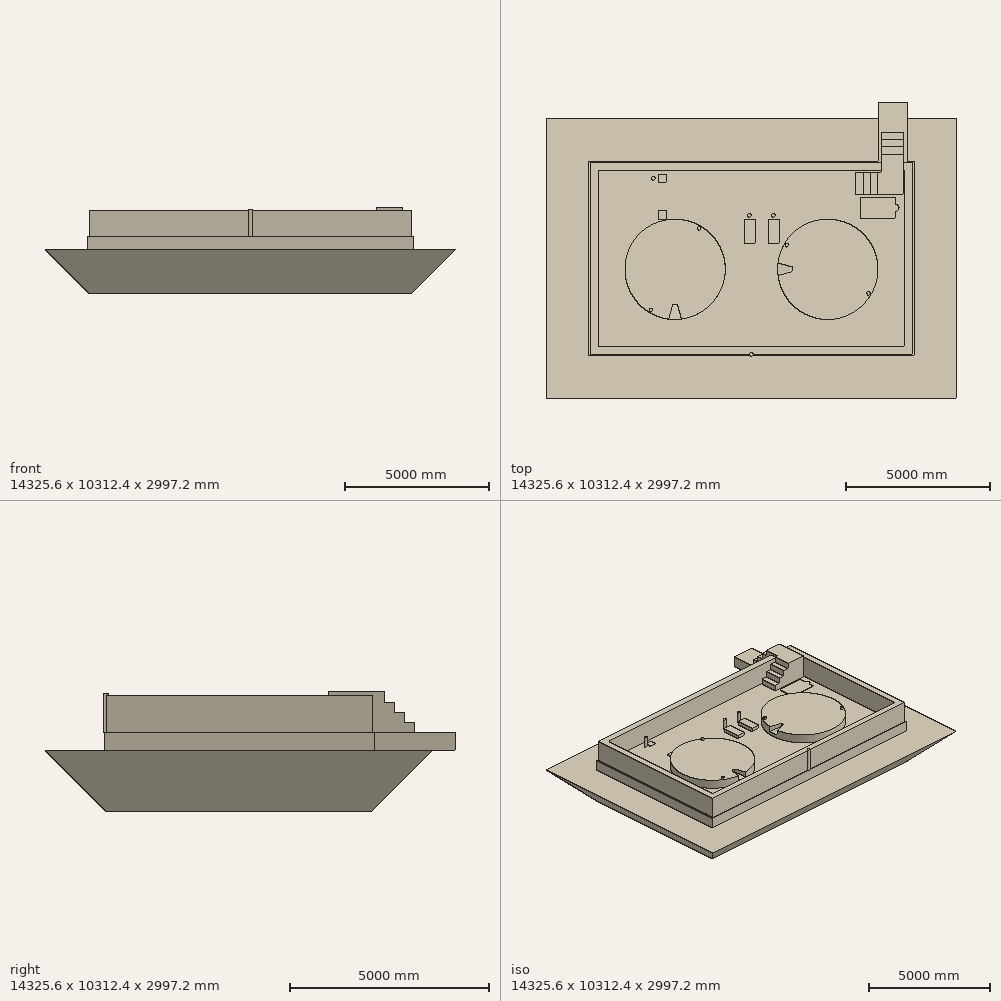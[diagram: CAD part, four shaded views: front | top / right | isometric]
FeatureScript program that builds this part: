
annotation { "Feature Type Name" : "Feature", "Feature Type Description" : "" }
export const myFeature = defineFeature(function(context is Context, id is Id, definition is map)
    precondition{}
    {
        {
            var Q0;
            Q0=qCreatedBy(makeId("Top.planeOp"),FACE);
            var sketch = newSketch(context, id + "F0", { "sketchPlane" : qUnion([Q0])});
            skLineSegment(sketch, "E0.bottom", {"start": v(5638.8, 3352.8) * mm, "end": v(-5638.8, 3352.8) * mm});
            skLineSegment(sketch, "E0.top", {"start": v(5638.8, -3352.8) * mm, "end": v(-5638.8, -3352.8) * mm});
            skLineSegment(sketch, "E0.left", {"start": v(5638.8, 3352.8) * mm, "end": v(5638.8, -3352.8) * mm});
            skLineSegment(sketch, "E0.right", {"start": v(-5638.8, 3352.8) * mm, "end": v(-5638.8, -3352.8) * mm});
            skPoint(sketch, "E0.middle", {"position": v(0, 0) * mm});
            skSolve(sketch);
        }
        {
            var Q0;
            Q0 = qSketchRegion(id + "F0", true);
            extrude(context, id + "F1", {"entities" : qUnion([Q0]), "oppositeDirection" : true, "depth" : 457.2 * mm});
        }
        {
            var Q0;
            Q0=makeQuery(id+"F1.opExtrude","CAP_FACE",FACE,{"disambiguationData":[OSD([sQuery(id+"F0.wireOp",EDGE,"E0.bottom"),sQuery(id+"F0.wireOp",EDGE,"E0.top"),sQuery(id+"F0.wireOp",EDGE,"E0.left"),sQuery(id+"F0.wireOp",EDGE,"E0.right")])],"isStart":true});
            var sketch = newSketch(context, id + "F2", { "sketchPlane" : qUnion([Q0])});
            skLineSegment(sketch, "E1.0.0", {"start": v(-5638.8, -3352.8) * mm, "end": v(5638.8, -3352.8) * mm});
            skLineSegment(sketch, "E1.0.1", {"start": v(5638.8, -3352.8) * mm, "end": v(5638.8, 3352.8) * mm});
            skLineSegment(sketch, "E1.0.2", {"start": v(5638.8, 3352.8) * mm, "end": v(-5638.8, 3352.8) * mm});
            skLineSegment(sketch, "E1.0.3", {"start": v(-5638.8, 3352.8) * mm, "end": v(-5638.8, -3352.8) * mm});
            skLineSegment(sketch, "E2.0", {"start": v(-5334, -3048) * mm, "end": v(5334, -3048) * mm});
            skLineSegment(sketch, "E2.1", {"start": v(-5334, 3048) * mm, "end": v(-5334, -3048) * mm});
            skLineSegment(sketch, "E2.2", {"start": v(5334, 3048) * mm, "end": v(-5334, 3048) * mm});
            skLineSegment(sketch, "E2.3", {"start": v(5334, -3048) * mm, "end": v(5334, 3048) * mm});
            skSolve(sketch);
        }
        {
            var Q0;
            Q0 = qSketchRegion(id + "F2", true);
            extrude(context, id + "F3", {"entities" : qUnion([Q0]), "depth" : 914.4 * mm});
        }
        {
            var Q0;
            Q0=makeQuery(id+"F1.opExtrude","CAP_FACE",FACE,{"disambiguationData":[OSD([sQuery(id+"F0.wireOp",EDGE,"E0.bottom"),sQuery(id+"F0.wireOp",EDGE,"E0.top"),sQuery(id+"F0.wireOp",EDGE,"E0.left"),sQuery(id+"F0.wireOp",EDGE,"E0.right")])],"isStart":true});
            var sketch = newSketch(context, id + "F4", { "sketchPlane" : qUnion([Q0])});
            skCircle(sketch, "E3.cCircle", {"center": v(-2667, -381) * mm, "radius": 1676.4 * mm, "construction": true});
            skLineSegment(sketch, "E3.0", {"start": v(-1972.61, 1295.4) * mm, "end": v(-990.6, 313.39) * mm, "construction": true});
            skLineSegment(sketch, "E3.1", {"start": v(-990.6, 313.39) * mm, "end": v(-990.6, -1075.39) * mm, "construction": true});
            skLineSegment(sketch, "E3.2", {"start": v(-990.6, -1075.39) * mm, "end": v(-1972.61, -2057.4) * mm, "construction": true});
            skLineSegment(sketch, "E3.3", {"start": v(-1972.61, -2057.4) * mm, "end": v(-3361.39, -2057.4) * mm, "construction": true});
            skLineSegment(sketch, "E3.4", {"start": v(-3361.39, -2057.4) * mm, "end": v(-4343.4, -1075.39) * mm, "construction": true});
            skLineSegment(sketch, "E3.5", {"start": v(-4343.4, -1075.39) * mm, "end": v(-4343.4, 313.39) * mm, "construction": true});
            skLineSegment(sketch, "E3.6", {"start": v(-4343.4, 313.39) * mm, "end": v(-3361.39, 1295.4) * mm, "construction": true});
            skLineSegment(sketch, "E3.7", {"start": v(-3361.39, 1295.4) * mm, "end": v(-1972.61, 1295.4) * mm, "construction": true});
            skPoint(sketch, "E3.0.midPoint", {"position": v(-1481.6, 804.4) * mm});
            skLineSegment(sketch, "E4", {"start": v(0, 0) * mm, "end": v(0, -381) * mm, "construction": true});
            skLineSegment(sketch, "E5", {"start": v(-2667, -381) * mm, "end": v(0, -381) * mm, "construction": true});
            skLineSegment(sketch, "E6.MirrorCS", {"start": v(3361.39, 1295.4) * mm, "end": v(1972.61, 1295.4) * mm, "construction": true});
            skPoint(sketch, "E7.MirrorP", {"position": v(1481.6, 804.4) * mm});
            skLineSegment(sketch, "E8.MirrorCS", {"start": v(4343.4, 313.39) * mm, "end": v(3361.39, 1295.4) * mm, "construction": true});
            skLineSegment(sketch, "E9.MirrorCS", {"start": v(4343.4, -1075.39) * mm, "end": v(4343.4, 313.39) * mm, "construction": true});
            skLineSegment(sketch, "E10.MirrorCS", {"start": v(3361.39, -2057.4) * mm, "end": v(4343.4, -1075.39) * mm, "construction": true});
            skLineSegment(sketch, "E11.MirrorCS", {"start": v(1972.61, -2057.4) * mm, "end": v(3361.39, -2057.4) * mm, "construction": true});
            skLineSegment(sketch, "E12.MirrorCS", {"start": v(990.6, -1075.39) * mm, "end": v(1972.61, -2057.4) * mm, "construction": true});
            skLineSegment(sketch, "E13.MirrorCS", {"start": v(1972.61, 1295.4) * mm, "end": v(990.6, 313.39) * mm, "construction": true});
            skLineSegment(sketch, "E14.MirrorCS", {"start": v(990.6, 313.39) * mm, "end": v(990.6, -1075.39) * mm, "construction": true});
            skCircle(sketch, "E15", {"center": v(-2667, -381) * mm, "radius": 1752.6 * mm});
            skCircle(sketch, "E16.MirrorC", {"center": v(2667, -381) * mm, "radius": 1752.6 * mm});
            skSolve(sketch);
        }
        {
            var Q0;
            Q0 = qSketchRegion(id + "F4", true);
            extrude(context, id + "F5", {"entities" : qUnion([Q0]), "depth" : 381 * mm});
        }
        {
            var Q0;
            Q0=makeQuery(id+"F1.opExtrude","CAP_FACE",FACE,{"disambiguationData":[OSD([sQuery(id+"F0.wireOp",EDGE,"E0.bottom"),sQuery(id+"F0.wireOp",EDGE,"E0.top"),sQuery(id+"F0.wireOp",EDGE,"E0.left"),sQuery(id+"F0.wireOp",EDGE,"E0.right")])],"isStart":true});
            var sketch = newSketch(context, id + "F6", { "sketchPlane" : qUnion([Q0])});
            skLineSegment(sketch, "E17.bottom", {"start": v(-2959.1, 2946.4) * mm, "end": v(-3263.9, 2946.4) * mm});
            skLineSegment(sketch, "E17.top", {"start": v(-2959.1, 2641.6) * mm, "end": v(-3263.9, 2641.6) * mm});
            skLineSegment(sketch, "E17.left", {"start": v(-2959.1, 2946.4) * mm, "end": v(-2959.1, 2641.6) * mm});
            skLineSegment(sketch, "E17.right", {"start": v(-3263.9, 2946.4) * mm, "end": v(-3263.9, 2641.6) * mm});
            skPoint(sketch, "E17.middle", {"position": v(-3111.5, 2794) * mm});
            skLineSegment(sketch, "E18.bottom", {"start": v(-2959.1, 1676.4) * mm, "end": v(-3263.9, 1676.4) * mm});
            skLineSegment(sketch, "E18.top", {"start": v(-2959.1, 1371.6) * mm, "end": v(-3263.9, 1371.6) * mm});
            skLineSegment(sketch, "E18.left", {"start": v(-2959.1, 1676.4) * mm, "end": v(-2959.1, 1371.6) * mm});
            skLineSegment(sketch, "E18.right", {"start": v(-3263.9, 1676.4) * mm, "end": v(-3263.9, 1371.6) * mm});
            skPoint(sketch, "E18.middle", {"position": v(-3111.5, 1524) * mm});
            skSolve(sketch);
        }
        {
            var Q0;
            Q0 = qSketchRegion(id + "F6", true);
            extrude(context, id + "F7", {"entities" : qUnion([Q0]), "depth" : 12.7 * mm});
        }
        {
            var Q0;
            Q0=makeQuery(id+"F1.opExtrude","CAP_FACE",FACE,{"disambiguationData":[OSD([sQuery(id+"F0.wireOp",EDGE,"E0.bottom"),sQuery(id+"F0.wireOp",EDGE,"E0.top"),sQuery(id+"F0.wireOp",EDGE,"E0.left"),sQuery(id+"F0.wireOp",EDGE,"E0.right")])],"isStart":true});
            var sketch = newSketch(context, id + "F8", { "sketchPlane" : qUnion([Q0])});
            skLineSegment(sketch, "E19.bottom", {"start": v(127, 1346.2) * mm, "end": v(-254, 1346.2) * mm});
            skLineSegment(sketch, "E19.top", {"start": v(127, 533.4) * mm, "end": v(-254, 533.4) * mm});
            skLineSegment(sketch, "E19.left", {"start": v(127, 1346.2) * mm, "end": v(127, 533.4) * mm});
            skLineSegment(sketch, "E19.right", {"start": v(-254, 1346.2) * mm, "end": v(-254, 533.4) * mm});
            skPoint(sketch, "E19.middle", {"position": v(-63.5, 939.8) * mm});
            skLineSegment(sketch, "E20.bottom", {"start": v(965.2, 1346.2) * mm, "end": v(584.2, 1346.2) * mm});
            skLineSegment(sketch, "E20.top", {"start": v(965.2, 533.4) * mm, "end": v(584.2, 533.4) * mm});
            skLineSegment(sketch, "E20.left", {"start": v(965.2, 1346.2) * mm, "end": v(965.2, 533.4) * mm});
            skLineSegment(sketch, "E20.right", {"start": v(584.2, 1346.2) * mm, "end": v(584.2, 533.4) * mm});
            skPoint(sketch, "E20.middle", {"position": v(774.7, 939.8) * mm});
            skLineSegment(sketch, "E21", {"start": v(965.2, -381) * mm, "end": v(914.4, -381) * mm, "construction": true});
            skLineSegment(sketch, "E22", {"start": v(965.2, -381) * mm, "end": v(965.2, 533.4) * mm, "construction": true});
            skPoint(sketch, "E23", {"position": v(-63.5, 1498.6) * mm});
            skPoint(sketch, "E24", {"position": v(774.7, 1498.6) * mm});
            skLineSegment(sketch, "E25", {"start": v(-63.5, 1498.6) * mm, "end": v(-63.5, 1346.2) * mm, "construction": true});
            skLineSegment(sketch, "E26", {"start": v(774.7, 1498.6) * mm, "end": v(774.7, 1346.2) * mm, "construction": true});
            skCircle(sketch, "E27.0", {"center": v(2667, -381) * mm, "radius": 1752.6 * mm, "construction": true});
            skLineSegment(sketch, "E28", {"start": v(965.2, 533.4) * mm, "end": v(1171.85, 533.4) * mm, "construction": true});
            skSolve(sketch);
        }
        {
            var Q0;
            Q0 = qSketchRegion(id + "F8", true);
            extrude(context, id + "F9", {"entities" : qUnion([Q0]), "depth" : 152.4 * mm});
        }
        {
            var Q0;
            Q0=makeQuery(id+"F1.opExtrude","CAP_FACE",FACE,{"disambiguationData":[OSD([sQuery(id+"F0.wireOp",EDGE,"E0.bottom"),sQuery(id+"F0.wireOp",EDGE,"E0.top"),sQuery(id+"F0.wireOp",EDGE,"E0.left"),sQuery(id+"F0.wireOp",EDGE,"E0.right")])],"isStart":false});
            cPlane(context, id + "F10", {"entities" : qUnion([Q0]), "cplaneType" : CPlaneType.OFFSET, "offset" : 1524 * mm, "width" : 152.4 * mm, "height" : 152.4 * mm});
        }
        {
            var Q0;
            Q0=qCreatedBy(id+"F10.planeOp",FACE);
            var sketch = newSketch(context, id + "F11", { "sketchPlane" : qUnion([Q0])});
            skLineSegment(sketch, "E29.0.0", {"start": v(5638.8, 3352.8) * mm, "end": v(-5638.8, 3352.8) * mm});
            skLineSegment(sketch, "E29.0.1", {"start": v(-5638.8, 3352.8) * mm, "end": v(-5638.8, -3352.8) * mm});
            skLineSegment(sketch, "E29.0.2", {"start": v(-5638.8, -3352.8) * mm, "end": v(5638.8, -3352.8) * mm});
            skLineSegment(sketch, "E29.0.3", {"start": v(5638.8, -3352.8) * mm, "end": v(5638.8, 3352.8) * mm});
            skSolve(sketch);
        }
        {
            var Q0;
            Q0 = qSketchRegion(id + "F11", true);
            extrude(context, id + "F12", {"entities" : qUnion([Q0]), "oppositeDirection" : true, "depth" : 1524 * mm, "hasDraft" : true, "draftAngle" : 45 * degree});
        }
        {
            var Q0;
            Q0=makeQuery(id+"F5.opExtrude","CAP_FACE",FACE,{"disambiguationData":[OSD([sQuery(id+"F4.wireOp",EDGE,"E15")])],"isStart":false});
            var sketch = newSketch(context, id + "F13", { "sketchPlane" : qUnion([Q0])});
            skCircle(sketch, "E30", {"center": v(-2667, -381) * mm, "radius": 1524 * mm, "construction": true});
            skLineSegment(sketch, "E31", {"start": v(-2667, -381) * mm, "end": v(-2667, 1371.6) * mm, "construction": true});
            skLineSegment(sketch, "E32", {"start": v(-2667, -381) * mm, "end": v(-2048.07, 1113.23) * mm, "construction": true});
            skCircle(sketch, "E33", {"center": v(-2048.07, 1113.23) * mm, "radius": 15.88 * mm});
            skLineSegment(sketch, "E34", {"start": v(-2154.92, 1054.4) * mm, "end": v(-2099.03, 1189.32) * mm, "construction": true});
            skLineSegment(sketch, "E35", {"start": v(-2099.03, 1189.32) * mm, "end": v(-1958.23, 1131) * mm, "construction": true});
            skLineSegment(sketch, "E36", {"start": v(-1958.23, 1131) * mm, "end": v(-2014.12, 996.07) * mm, "construction": true});
            skLineSegment(sketch, "E37", {"start": v(-2028.63, 1160.16) * mm, "end": v(-2048.07, 1113.23) * mm, "construction": true});
            skLineSegment(sketch, "E38.1.0", {"start": v(-3305.37, 1160.16) * mm, "end": v(-3285.93, 1113.23) * mm, "construction": true});
            skCircle(sketch, "E38.1.1", {"center": v(-3285.93, 1113.23) * mm, "radius": 15.88 * mm});
            skLineSegment(sketch, "E38.1.2", {"start": v(-3234.97, 1189.32) * mm, "end": v(-3179.08, 1054.4) * mm, "construction": true});
            skLineSegment(sketch, "E38.1.3", {"start": v(-3319.88, 996.07) * mm, "end": v(-3375.77, 1131) * mm, "construction": true});
            skLineSegment(sketch, "E38.1.4", {"start": v(-3375.77, 1131) * mm, "end": v(-3234.97, 1189.32) * mm, "construction": true});
            skLineSegment(sketch, "E38.2.0", {"start": v(-4208.16, 257.37) * mm, "end": v(-4161.23, 237.93) * mm, "construction": true});
            skCircle(sketch, "E38.2.1", {"center": v(-4161.23, 237.93) * mm, "radius": 15.88 * mm});
            skLineSegment(sketch, "E38.2.2", {"start": v(-4179, 327.77) * mm, "end": v(-4044.07, 271.88) * mm, "construction": true});
            skLineSegment(sketch, "E38.2.3", {"start": v(-4102.4, 131.08) * mm, "end": v(-4237.32, 186.97) * mm, "construction": true});
            skLineSegment(sketch, "E38.2.4", {"start": v(-4237.32, 186.97) * mm, "end": v(-4179, 327.77) * mm, "construction": true});
            skLineSegment(sketch, "E38.3.0", {"start": v(-4208.16, -1019.37) * mm, "end": v(-4161.23, -999.93) * mm, "construction": true});
            skCircle(sketch, "E38.3.1", {"center": v(-4161.23, -999.93) * mm, "radius": 15.88 * mm});
            skLineSegment(sketch, "E38.3.2", {"start": v(-4237.32, -948.97) * mm, "end": v(-4102.4, -893.08) * mm, "construction": true});
            skLineSegment(sketch, "E38.3.3", {"start": v(-4044.07, -1033.88) * mm, "end": v(-4179, -1089.77) * mm, "construction": true});
            skLineSegment(sketch, "E38.3.4", {"start": v(-4179, -1089.77) * mm, "end": v(-4237.32, -948.97) * mm, "construction": true});
            skLineSegment(sketch, "E38.4.0", {"start": v(-3305.37, -1922.16) * mm, "end": v(-3285.93, -1875.23) * mm, "construction": true});
            skCircle(sketch, "E38.4.1", {"center": v(-3285.93, -1875.23) * mm, "radius": 15.88 * mm});
            skLineSegment(sketch, "E38.4.2", {"start": v(-3375.77, -1893) * mm, "end": v(-3319.88, -1758.07) * mm, "construction": true});
            skLineSegment(sketch, "E38.4.3", {"start": v(-3179.08, -1816.4) * mm, "end": v(-3234.97, -1951.32) * mm, "construction": true});
            skLineSegment(sketch, "E38.4.4", {"start": v(-3234.97, -1951.32) * mm, "end": v(-3375.77, -1893) * mm, "construction": true});
            skLineSegment(sketch, "E38.5.0", {"start": v(-2028.63, -1922.16) * mm, "end": v(-2048.07, -1875.23) * mm, "construction": true});
            skCircle(sketch, "E38.5.1", {"center": v(-2048.07, -1875.23) * mm, "radius": 15.88 * mm});
            skLineSegment(sketch, "E38.5.2", {"start": v(-2099.03, -1951.32) * mm, "end": v(-2154.92, -1816.4) * mm, "construction": true});
            skLineSegment(sketch, "E38.5.3", {"start": v(-2014.12, -1758.07) * mm, "end": v(-1958.23, -1893) * mm, "construction": true});
            skLineSegment(sketch, "E38.5.4", {"start": v(-1958.23, -1893) * mm, "end": v(-2099.03, -1951.32) * mm, "construction": true});
            skLineSegment(sketch, "E38.6.0", {"start": v(-1125.84, -1019.37) * mm, "end": v(-1172.77, -999.93) * mm, "construction": true});
            skCircle(sketch, "E38.6.1", {"center": v(-1172.77, -999.93) * mm, "radius": 15.88 * mm});
            skLineSegment(sketch, "E38.6.2", {"start": v(-1155, -1089.77) * mm, "end": v(-1289.93, -1033.88) * mm, "construction": true});
            skLineSegment(sketch, "E38.6.3", {"start": v(-1231.6, -893.08) * mm, "end": v(-1096.68, -948.97) * mm, "construction": true});
            skLineSegment(sketch, "E38.6.4", {"start": v(-1096.68, -948.97) * mm, "end": v(-1155, -1089.77) * mm, "construction": true});
            skLineSegment(sketch, "E38.7.0", {"start": v(-1125.84, 257.37) * mm, "end": v(-1172.77, 237.93) * mm, "construction": true});
            skCircle(sketch, "E38.7.1", {"center": v(-1172.77, 237.93) * mm, "radius": 15.88 * mm});
            skLineSegment(sketch, "E38.7.2", {"start": v(-1096.68, 186.97) * mm, "end": v(-1231.6, 131.08) * mm, "construction": true});
            skLineSegment(sketch, "E38.7.3", {"start": v(-1289.93, 271.88) * mm, "end": v(-1155, 327.77) * mm, "construction": true});
            skLineSegment(sketch, "E38.7.4", {"start": v(-1155, 327.77) * mm, "end": v(-1096.68, 186.97) * mm, "construction": true});
            skLineSegment(sketch, "E39", {"start": v(0, 0) * mm, "end": v(0, 605.74) * mm, "construction": true});
            skLineSegment(sketch, "E40.MirrorCS", {"start": v(2099.03, 1189.32) * mm, "end": v(1958.23, 1131) * mm, "construction": true});
            skLineSegment(sketch, "E41.MirrorCS", {"start": v(2154.92, 1054.4) * mm, "end": v(2099.03, 1189.32) * mm, "construction": true});
            skCircle(sketch, "E42.MirrorC", {"center": v(2048.07, 1113.23) * mm, "radius": 15.88 * mm});
            skLineSegment(sketch, "E43.MirrorCS", {"start": v(1958.23, 1131) * mm, "end": v(2014.12, 996.07) * mm, "construction": true});
            skLineSegment(sketch, "E44.MirrorCS", {"start": v(2028.63, 1160.16) * mm, "end": v(2048.07, 1113.23) * mm, "construction": true});
            skLineSegment(sketch, "E45.MirrorCS", {"start": v(1155, 327.77) * mm, "end": v(1096.68, 186.97) * mm, "construction": true});
            skLineSegment(sketch, "E46.MirrorCS", {"start": v(1125.84, 257.37) * mm, "end": v(1172.77, 237.93) * mm, "construction": true});
            skCircle(sketch, "E47.MirrorC", {"center": v(3285.93, -1875.23) * mm, "radius": 15.88 * mm});
            skCircle(sketch, "E48.MirrorC", {"center": v(1172.77, 237.93) * mm, "radius": 15.88 * mm});
            skCircle(sketch, "E49.MirrorC", {"center": v(3285.93, 1113.23) * mm, "radius": 15.88 * mm});
            skLineSegment(sketch, "E50.MirrorCS", {"start": v(4179, 327.77) * mm, "end": v(4044.07, 271.88) * mm, "construction": true});
            skCircle(sketch, "E51.MirrorC", {"center": v(4161.23, 237.93) * mm, "radius": 15.88 * mm});
            skLineSegment(sketch, "E52.MirrorCS", {"start": v(1958.23, -1893) * mm, "end": v(2099.03, -1951.32) * mm, "construction": true});
            skLineSegment(sketch, "E53.MirrorCS", {"start": v(4208.16, 257.37) * mm, "end": v(4161.23, 237.93) * mm, "construction": true});
            skLineSegment(sketch, "E54.MirrorCS", {"start": v(4102.4, 131.08) * mm, "end": v(4237.32, 186.97) * mm, "construction": true});
            skCircle(sketch, "E55.MirrorC", {"center": v(2048.07, -1875.23) * mm, "radius": 15.88 * mm});
            skLineSegment(sketch, "E56.MirrorCS", {"start": v(1231.6, -893.08) * mm, "end": v(1096.68, -948.97) * mm, "construction": true});
            skLineSegment(sketch, "E57.MirrorCS", {"start": v(4237.32, -948.97) * mm, "end": v(4102.4, -893.08) * mm, "construction": true});
            skLineSegment(sketch, "E58.MirrorCS", {"start": v(3179.08, -1816.4) * mm, "end": v(3234.97, -1951.32) * mm, "construction": true});
            skLineSegment(sketch, "E59.MirrorCS", {"start": v(1155, -1089.77) * mm, "end": v(1289.93, -1033.88) * mm, "construction": true});
            skCircle(sketch, "E60.MirrorC", {"center": v(4161.23, -999.93) * mm, "radius": 15.88 * mm});
            skLineSegment(sketch, "E61.MirrorCS", {"start": v(3375.77, -1893) * mm, "end": v(3319.88, -1758.07) * mm, "construction": true});
            skLineSegment(sketch, "E62.MirrorCS", {"start": v(1289.93, 271.88) * mm, "end": v(1155, 327.77) * mm, "construction": true});
            skLineSegment(sketch, "E63.MirrorCS", {"start": v(4179, -1089.77) * mm, "end": v(4237.32, -948.97) * mm, "construction": true});
            skCircle(sketch, "E64.MirrorC", {"center": v(1172.77, -999.93) * mm, "radius": 15.88 * mm});
            skLineSegment(sketch, "E65.MirrorCS", {"start": v(4208.16, -1019.37) * mm, "end": v(4161.23, -999.93) * mm, "construction": true});
            skLineSegment(sketch, "E66.MirrorCS", {"start": v(2014.12, -1758.07) * mm, "end": v(1958.23, -1893) * mm, "construction": true});
            skLineSegment(sketch, "E67.MirrorCS", {"start": v(1096.68, 186.97) * mm, "end": v(1231.6, 131.08) * mm, "construction": true});
            skLineSegment(sketch, "E68.MirrorCS", {"start": v(2028.63, -1922.16) * mm, "end": v(2048.07, -1875.23) * mm, "construction": true});
            skLineSegment(sketch, "E69.MirrorCS", {"start": v(1125.84, -1019.37) * mm, "end": v(1172.77, -999.93) * mm, "construction": true});
            skLineSegment(sketch, "E70.MirrorCS", {"start": v(4237.32, 186.97) * mm, "end": v(4179, 327.77) * mm, "construction": true});
            skLineSegment(sketch, "E71.MirrorCS", {"start": v(1096.68, -948.97) * mm, "end": v(1155, -1089.77) * mm, "construction": true});
            skLineSegment(sketch, "E72.MirrorCS", {"start": v(2099.03, -1951.32) * mm, "end": v(2154.92, -1816.4) * mm, "construction": true});
            skLineSegment(sketch, "E73.MirrorCS", {"start": v(4044.07, -1033.88) * mm, "end": v(4179, -1089.77) * mm, "construction": true});
            skLineSegment(sketch, "E74.MirrorCS", {"start": v(3305.37, -1922.16) * mm, "end": v(3285.93, -1875.23) * mm, "construction": true});
            skLineSegment(sketch, "E75.MirrorCS", {"start": v(3234.97, -1951.32) * mm, "end": v(3375.77, -1893) * mm, "construction": true});
            skLineSegment(sketch, "E76.MirrorCS", {"start": v(3234.97, 1189.32) * mm, "end": v(3179.08, 1054.4) * mm, "construction": true});
            skLineSegment(sketch, "E77.MirrorCS", {"start": v(3375.77, 1131) * mm, "end": v(3234.97, 1189.32) * mm, "construction": true});
            skLineSegment(sketch, "E78.MirrorCS", {"start": v(3305.37, 1160.16) * mm, "end": v(3285.93, 1113.23) * mm, "construction": true});
            skLineSegment(sketch, "E79.MirrorCS", {"start": v(3319.88, 996.07) * mm, "end": v(3375.77, 1131) * mm, "construction": true});
            skLineSegment(sketch, "E80.MirrorCS", {"start": v(2667, -381) * mm, "end": v(2667, 1371.6) * mm, "construction": true});
            skLineSegment(sketch, "E81.MirrorCS", {"start": v(2667, -381) * mm, "end": v(2048.07, 1113.23) * mm, "construction": true});
            skCircle(sketch, "E82.MirrorC", {"center": v(2667, -381) * mm, "radius": 1524 * mm, "construction": true});
            skCircle(sketch, "E83", {"center": v(-2667, -381) * mm, "radius": 1574.8 * mm});
            skCircle(sketch, "E84", {"center": v(2667, -381) * mm, "radius": 1574.8 * mm});
            skSolve(sketch);
        }
        {
            var Q0;
            Q0=makeQuery(id+"F1.opExtrude","CAP_FACE",FACE,{"disambiguationData":[OSD([sQuery(id+"F0.wireOp",EDGE,"E0.bottom"),sQuery(id+"F0.wireOp",EDGE,"E0.top"),sQuery(id+"F0.wireOp",EDGE,"E0.left"),sQuery(id+"F0.wireOp",EDGE,"E0.right")])],"isStart":true});
            var sketch = newSketch(context, id + "F14", { "sketchPlane" : qUnion([Q0])});
            skCircle(sketch, "E85", {"center": v(-63.5, 1498.6) * mm, "radius": 63.5 * mm});
            skCircle(sketch, "E86", {"center": v(774.7, 1498.6) * mm, "radius": 63.5 * mm});
            skCircle(sketch, "E87", {"center": v(4097.22, -1220.85) * mm, "radius": 63.5 * mm});
            skCircle(sketch, "E88", {"center": v(-3416.3, 2794) * mm, "radius": 63.5 * mm});
            skCircle(sketch, "E89", {"center": v(0, -3352.8) * mm, "radius": 63.5 * mm});
            skLineSegment(sketch, "E90", {"start": v(-3416.3, 2794) * mm, "end": v(-3263.9, 2794) * mm, "construction": true});
            skLineSegment(sketch, "E91", {"start": v(4097.22, -1220.85) * mm, "end": v(4155.54, -1080.05) * mm, "construction": true});
            skCircle(sketch, "E92", {"center": v(1236.78, 458.85) * mm, "radius": 63.5 * mm});
            skLineSegment(sketch, "E93", {"start": v(1178.46, 318.05) * mm, "end": v(1236.78, 458.85) * mm, "construction": true});
            skCircle(sketch, "E94", {"center": v(-3506.85, -1811.22) * mm, "radius": 63.5 * mm});
            skLineSegment(sketch, "E95", {"start": v(-3366.05, -1869.54) * mm, "end": v(-3506.85, -1811.22) * mm, "construction": true});
            skCircle(sketch, "E96", {"center": v(-1827.15, 1049.22) * mm, "radius": 63.5 * mm});
            skLineSegment(sketch, "E97", {"start": v(-1967.95, 1107.54) * mm, "end": v(-1827.15, 1049.22) * mm, "construction": true});
            skSolve(sketch);
        }
        {
            var Q0;
            Q0 = qSketchRegion(id + "F14", true);
            extrude(context, id + "F15", {"entities" : qUnion([Q0]), "depth" : 457.2 * mm});
        }
        {
            var Q0;
            Q0=makeQuery(id+"F15.opExtrude","CAP_FACE",FACE,{"disambiguationData":[OSD([sQuery(id+"F14.wireOp",EDGE,"E89")])],"isStart":false});
            extrude(context, id + "F16", {"entities" : qUnion([Q0]), "operationType" : NewBodyOperationType.ADD, "depth" : 508 * mm});
        }
        {
            var Q0;
            Q0=makeQuery(id+"F3.opExtrude","CAP_FACE",FACE,{"disambiguationData":[OSD([sQuery(id+"F2.wireOp",EDGE,"E1.0.0"),sQuery(id+"F2.wireOp",EDGE,"E1.0.1"),sQuery(id+"F2.wireOp",EDGE,"E1.0.2"),sQuery(id+"F2.wireOp",EDGE,"E1.0.3"),sQuery(id+"F2.wireOp",EDGE,"E2.0"),sQuery(id+"F2.wireOp",EDGE,"E2.1"),sQuery(id+"F2.wireOp",EDGE,"E2.2"),sQuery(id+"F2.wireOp",EDGE,"E2.3")])],"isStart":false});
            var sketch = newSketch(context, id + "F17", { "sketchPlane" : qUnion([Q0])});
            skLineSegment(sketch, "E98.0", {"start": v(-5334, 3048) * mm, "end": v(-5334, -3048) * mm});
            skLineSegment(sketch, "E99.0", {"start": v(5334, 3048) * mm, "end": v(-5334, 3048) * mm});
            skLineSegment(sketch, "E100.0", {"start": v(5334, -3048) * mm, "end": v(5334, 3048) * mm});
            skLineSegment(sketch, "E101.0", {"start": v(-5334, -3048) * mm, "end": v(5334, -3048) * mm});
            skLineSegment(sketch, "E102.0", {"start": v(-5346.7, 3060.7) * mm, "end": v(-5346.7, -3060.7) * mm});
            skLineSegment(sketch, "E102.1", {"start": v(5346.7, 3060.7) * mm, "end": v(-5346.7, 3060.7) * mm});
            skLineSegment(sketch, "E102.2", {"start": v(5346.7, -3060.7) * mm, "end": v(5346.7, 3060.7) * mm});
            skLineSegment(sketch, "E102.3", {"start": v(-5346.7, -3060.7) * mm, "end": v(5346.7, -3060.7) * mm});
            skSolve(sketch);
        }
        {
            var Q0;
            Q0 = qSketchRegion(id + "F17", true);
            var Q1;
            Q1=makeQuery(id+"F1.opExtrude","CAP_FACE",FACE,{"disambiguationData":[OSD([sQuery(id+"F0.wireOp",EDGE,"E0.bottom"),sQuery(id+"F0.wireOp",EDGE,"E0.top"),sQuery(id+"F0.wireOp",EDGE,"E0.left"),sQuery(id+"F0.wireOp",EDGE,"E0.right")])],"isStart":true});
            extrude(context, id + "F18", {"entities" : qUnion([Q0]), "operationType" : NewBodyOperationType.REMOVE, "endBound" : BoundingType.UP_TO_SURFACE, "oppositeDirection" : true, "endBoundEntityFace" : qUnion([Q1]), "depth" : 25.4 * mm});
        }
        {
            var Q0;
            Q0=makeQuery(id+"F5.opExtrude","CAP_FACE",FACE,{"disambiguationData":[OSD([sQuery(id+"F4.wireOp",EDGE,"E15")])],"isStart":false});
            var sketch = newSketch(context, id + "F19", { "sketchPlane" : qUnion([Q0])});
            skLineSegment(sketch, "E103.bottom", {"start": v(-2628.9, -1752.6) * mm, "end": v(-2705.1, -1752.6) * mm, "construction": true});
            skLineSegment(sketch, "E103.top", {"start": v(-2628.9, -2006.6) * mm, "end": v(-2705.1, -2006.6) * mm, "construction": true});
            skLineSegment(sketch, "E103.left", {"start": v(-2628.9, -1752.6) * mm, "end": v(-2628.9, -2006.6) * mm, "construction": true});
            skLineSegment(sketch, "E103.right", {"start": v(-2705.1, -1752.6) * mm, "end": v(-2705.1, -2006.6) * mm, "construction": true});
            skPoint(sketch, "E103.middle", {"position": v(-2667, -1879.6) * mm});
            skLineSegment(sketch, "E104", {"start": v(-2667, -381) * mm, "end": v(-2667, -1879.6) * mm, "construction": true});
            skLineSegment(sketch, "E105.bottom", {"start": v(-2762.25, -1982.72) * mm, "end": v(-2571.75, -1982.72) * mm, "construction": true});
            skLineSegment(sketch, "E105.top", {"start": v(-2762.25, -2006.6) * mm, "end": v(-2571.75, -2006.6) * mm, "construction": true});
            skLineSegment(sketch, "E105.left", {"start": v(-2762.25, -1982.72) * mm, "end": v(-2762.25, -2006.6) * mm, "construction": true});
            skLineSegment(sketch, "E105.right", {"start": v(-2571.75, -1982.72) * mm, "end": v(-2571.75, -2006.6) * mm, "construction": true});
            skPoint(sketch, "E106", {"position": v(-2667, -2006.6) * mm});
            skSolve(sketch);
        }
        {
            var Q0;
            Q0=makeQuery(id+"F19.imprint","IMPRINT",FACE,{"disambiguationData":[TD([[makeQuery(id+"F19.imprint","IMPRINT",EDGE,{"derivedFrom":makeQuery(id+"F5.opExtrude","CAP_EDGE",EDGE,{"disambiguationData":[OSD([sQuery(id+"F4.wireOp",EDGE,"E15")])],"isStart":false})}),1.0]])]});
            var sketch = newSketch(context, id + "F20", { "sketchPlane" : qUnion([Q0])});
            skLineSegment(sketch, "E107", {"start": v(-2895.6, -2133.6) * mm, "end": v(-2743.2, -1600.2) * mm});
            skLineSegment(sketch, "E108", {"start": v(-2743.2, -1600.2) * mm, "end": v(-2590.8, -1600.2) * mm});
            skLineSegment(sketch, "E109", {"start": v(-2590.8, -1600.2) * mm, "end": v(-2438.4, -2133.6) * mm});
            skPoint(sketch, "E110", {"position": v(-2667, -1600.2) * mm});
            skLineSegment(sketch, "E111", {"start": v(-2895.6, -2133.6) * mm, "end": v(-2438.4, -2133.6) * mm});
            skLineSegment(sketch, "E112", {"start": v(914.4, -152.4) * mm, "end": v(1447.8, -304.8) * mm});
            skLineSegment(sketch, "E113", {"start": v(1447.8, -304.8) * mm, "end": v(1447.8, -457.2) * mm});
            skLineSegment(sketch, "E114", {"start": v(1447.8, -457.2) * mm, "end": v(914.4, -609.6) * mm});
            skPoint(sketch, "E115", {"position": v(1447.8, -381) * mm});
            skLineSegment(sketch, "E116", {"start": v(914.4, -152.4) * mm, "end": v(914.4, -609.6) * mm});
            skLineSegment(sketch, "E117", {"start": v(1447.8, -381) * mm, "end": v(2667, -381) * mm, "construction": true});
            skCircle(sketch, "E118.0", {"center": v(2667, -381) * mm, "radius": 1752.6 * mm, "construction": true});
            skSolve(sketch);
        }
        {
            var Q0;
            Q0 = qSketchRegion(id + "F20", true);
            extrude(context, id + "F21", {"entities" : qUnion([Q0]), "operationType" : NewBodyOperationType.REMOVE, "oppositeDirection" : true, "depth" : 228.6 * mm});
        }
        {
            var Q0;
            Q0=makeQuery(id+"F21.boolean.opBoolean","COPY",EDGE,{"derivedFrom":makeQuery(id+"F21.opExtrude","CAP_EDGE",EDGE,{"disambiguationData":[OSD([sQuery(id+"F20.wireOp",EDGE,"E108")])],"isStart":false})});
            var Q1;
            Q1=makeQuery(id+"F21.boolean.opBoolean","COPY",EDGE,{"derivedFrom":makeQuery(id+"F21.opExtrude","CAP_EDGE",EDGE,{"disambiguationData":[OSD([sQuery(id+"F20.wireOp",EDGE,"E113")])],"isStart":false})});
            chamfer(context, id + "F22", {"entities" : qUnion([Q0, Q1]), "chamferType" : ChamferType.TWO_OFFSETS, "width1" : 76.2 * mm, "oppositeDirection" : false, "width2" : 533.4 * mm});
        }
        {
            var Q0;
            Q0=qCreatedBy(makeId("Top.planeOp"),FACE);
            var sketch = newSketch(context, id + "F23", { "sketchPlane" : qUnion([Q0])});
            skLineSegment(sketch, "E119.0.0", {"start": v(5638.8, -3352.8) * mm, "end": v(-5638.8, -3352.8) * mm});
            skLineSegment(sketch, "E119.0.1", {"start": v(-5638.8, -3352.8) * mm, "end": v(-5638.8, 3352.8) * mm});
            skLineSegment(sketch, "E119.0.2", {"start": v(-5638.8, 3352.8) * mm, "end": v(5638.8, 3352.8) * mm});
            skLineSegment(sketch, "E119.0.3", {"start": v(5638.8, 3352.8) * mm, "end": v(5638.8, -3352.8) * mm});
            skLineSegment(sketch, "E120.0", {"start": v(5689.6, -3403.6) * mm, "end": v(-5689.6, -3403.6) * mm});
            skLineSegment(sketch, "E120.1", {"start": v(5689.6, 3403.6) * mm, "end": v(5689.6, -3403.6) * mm});
            skLineSegment(sketch, "E120.2", {"start": v(-5689.6, 3403.6) * mm, "end": v(5689.6, 3403.6) * mm});
            skLineSegment(sketch, "E120.3", {"start": v(-5689.6, -3403.6) * mm, "end": v(-5689.6, 3403.6) * mm});
            skSolve(sketch);
        }
        {
            var Q0;
            Q0 = qSketchRegion(id + "F23", true);
            var Q1;
            Q1=makeQuery(id+"F1.opExtrude","CAP_FACE",FACE,{"disambiguationData":[OSD([sQuery(id+"F0.wireOp",EDGE,"E0.bottom"),sQuery(id+"F0.wireOp",EDGE,"E0.top"),sQuery(id+"F0.wireOp",EDGE,"E0.left"),sQuery(id+"F0.wireOp",EDGE,"E0.right")])],"isStart":false});
            extrude(context, id + "F24", {"entities" : qUnion([Q0]), "operationType" : NewBodyOperationType.ADD, "endBound" : BoundingType.UP_TO_SURFACE, "oppositeDirection" : true, "endBoundEntityFace" : qUnion([Q1]), "depth" : 25.4 * mm});
        }
        {
            var Q0;
            Q0=makeQuery(id+"F24.opExtrude","SWEPT_FACE",FACE,{"disambiguationData":[OSD([sQuery(id+"F23.wireOp",EDGE,"E120.2")])]});
            var sketch = newSketch(context, id + "F25", { "sketchPlane" : qUnion([Q0])});
            skLineSegment(sketch, "E121.bottom", {"start": v(-5461, 0) * mm, "end": v(-4445, 0) * mm});
            skLineSegment(sketch, "E121.top", {"start": v(-5461, -457.2) * mm, "end": v(-4445, -457.2) * mm});
            skLineSegment(sketch, "E121.left", {"start": v(-4445, 0) * mm, "end": v(-4445, -457.2) * mm});
            skLineSegment(sketch, "E121.right", {"start": v(-5461, 0) * mm, "end": v(-5461, -457.2) * mm});
            skLineSegment(sketch, "E122", {"start": v(-4953, -149.85) * mm, "end": v(-4953, 0) * mm, "construction": true});
            skPoint(sketch, "E122.startSnap0", {"position": v(-4953, 0) * mm});
            skSolve(sketch);
        }
        {
            var Q0;
            Q0 = qSketchRegion(id + "F25", true);
            extrude(context, id + "F26", {"entities" : qUnion([Q0]), "operationType" : NewBodyOperationType.ADD, "depth" : 2032 * mm});
        }
        {
            var Q0;
            Q0=makeQuery(id+"F18.boolean.opBoolean","COPY",FACE,{"derivedFrom":makeQuery(id+"F18.opExtrude","SWEPT_FACE",FACE,{"disambiguationData":[OSD([sQuery(id+"F17.wireOp",EDGE,"E102.0")])]})});
            var sketch = newSketch(context, id + "F27", { "sketchPlane" : qUnion([Q0])});
            skCircle(sketch, "E123", {"center": v(-2984.5, 28.57) * mm, "radius": 25.4 * mm});
            skSolve(sketch);
        }
        {
            var Q0;
            Q0 = qSketchRegion(id + "F27", true);
            extrude(context, id + "F28", {"entities" : qUnion([Q0]), "operationType" : NewBodyOperationType.REMOVE, "endBound" : BoundingType.THROUGH_ALL, "oppositeDirection" : true, "depth" : 25.4 * mm});
        }
        {
            var Q0;
            Q0=makeQuery(id+"F26.boolean.opBoolean","MERGE",FACE,{"derivedFrom":[makeQuery(id+"F24.boolean.opBoolean","MERGE",FACE,{"derivedFrom":[makeQuery(id+"F1.opExtrude","CAP_FACE",FACE,{"disambiguationData":[OSD([sQuery(id+"F0.wireOp",EDGE,"E0.bottom"),sQuery(id+"F0.wireOp",EDGE,"E0.top"),sQuery(id+"F0.wireOp",EDGE,"E0.left"),sQuery(id+"F0.wireOp",EDGE,"E0.right")])],"isStart":true}),makeQuery(id+"F24.opExtrude","CAP_FACE",FACE,{"disambiguationData":[OSD([sQuery(id+"F23.wireOp",EDGE,"E119.0.0"),sQuery(id+"F23.wireOp",EDGE,"E119.0.1"),sQuery(id+"F23.wireOp",EDGE,"E119.0.2"),sQuery(id+"F23.wireOp",EDGE,"E119.0.3"),sQuery(id+"F23.wireOp",EDGE,"E120.0"),sQuery(id+"F23.wireOp",EDGE,"E120.1"),sQuery(id+"F23.wireOp",EDGE,"E120.2"),sQuery(id+"F23.wireOp",EDGE,"E120.3")])],"isStart":true})]}),makeQuery(id+"F26.opExtrude","SWEPT_FACE",FACE,{"disambiguationData":[OSD([sQuery(id+"F25.wireOp",EDGE,"E121.bottom")])]})]});
            var sketch = newSketch(context, id + "F29", { "sketchPlane" : qUnion([Q0])});
            skLineSegment(sketch, "E124.bottom", {"start": v(3644.9, 2247.9) * mm, "end": v(5295.9, 2247.9) * mm});
            skLineSegment(sketch, "E124.top", {"start": v(3644.9, 3009.9) * mm, "end": v(4533.9, 3009.9) * mm});
            skLineSegment(sketch, "E124.left", {"start": v(3644.9, 2247.9) * mm, "end": v(3644.9, 3009.9) * mm});
            skLineSegment(sketch, "E125.top", {"start": v(5295.9, 4406.9) * mm, "end": v(4533.9, 4406.9) * mm});
            skLineSegment(sketch, "E126", {"start": v(4533.9, 4406.9) * mm, "end": v(4533.9, 3009.9) * mm});
            skLineSegment(sketch, "E127", {"start": v(5295.9, 4406.9) * mm, "end": v(5295.9, 2247.9) * mm});
            skSolve(sketch);
        }
        {
            var Q0;
            Q0 = qSketchRegion(id + "F29", true);
            extrude(context, id + "F30", {"entities" : qUnion([Q0]), "depth" : 1016 * mm});
        }
        {
            var Q0;
            Q0=makeQuery(id+"F30.opExtrude","SWEPT_FACE",FACE,{"disambiguationData":[OSD([sQuery(id+"F29.wireOp",EDGE,"E127")])]});
            var sketch = newSketch(context, id + "F31", { "sketchPlane" : qUnion([Q0])});
            skLineSegment(sketch, "E128", {"start": v(4406.9, 254) * mm, "end": v(4406.9, 1016) * mm});
            skLineSegment(sketch, "E129", {"start": v(4406.9, 1016) * mm, "end": v(3644.9, 1016) * mm});
            skLineSegment(sketch, "E130", {"start": v(3644.9, 1016) * mm, "end": v(3644.9, 762) * mm});
            skLineSegment(sketch, "E131", {"start": v(3644.9, 762) * mm, "end": v(3898.9, 762) * mm});
            skLineSegment(sketch, "E132", {"start": v(3898.9, 762) * mm, "end": v(3898.9, 508) * mm});
            skLineSegment(sketch, "E133", {"start": v(3898.9, 508) * mm, "end": v(4152.9, 508) * mm});
            skLineSegment(sketch, "E134", {"start": v(4152.9, 508) * mm, "end": v(4152.9, 254) * mm});
            skLineSegment(sketch, "E135", {"start": v(4152.9, 254) * mm, "end": v(4406.9, 254) * mm});
            skLineSegment(sketch, "E136", {"start": v(4406.9, 254) * mm, "end": v(4406.9, 0) * mm, "construction": true});
            skSolve(sketch);
        }
        {
            var Q0;
            Q0 = qSketchRegion(id + "F31", true);
            extrude(context, id + "F32", {"entities" : qUnion([Q0]), "operationType" : NewBodyOperationType.REMOVE, "oppositeDirection" : true, "depth" : 762 * mm});
        }
        {
            var Q0;
            Q0=makeQuery(id+"F30.opExtrude","SWEPT_FACE",FACE,{"disambiguationData":[OSD([sQuery(id+"F29.wireOp",EDGE,"E124.top")])]});
            var sketch = newSketch(context, id + "F33", { "sketchPlane" : qUnion([Q0])});
            skLineSegment(sketch, "E137", {"start": v(-3644.9, 254) * mm, "end": v(-3644.9, 1016) * mm});
            skLineSegment(sketch, "E138", {"start": v(-3644.9, 1016) * mm, "end": v(-4406.9, 1016) * mm});
            skLineSegment(sketch, "E139", {"start": v(-4406.9, 1016) * mm, "end": v(-4406.9, 762) * mm});
            skLineSegment(sketch, "E140", {"start": v(-4406.9, 762) * mm, "end": v(-4152.9, 762) * mm});
            skLineSegment(sketch, "E141", {"start": v(-4152.9, 762) * mm, "end": v(-4152.9, 508) * mm});
            skLineSegment(sketch, "E142", {"start": v(-4152.9, 508) * mm, "end": v(-3898.9, 508) * mm});
            skLineSegment(sketch, "E143", {"start": v(-3898.9, 508) * mm, "end": v(-3898.9, 254) * mm});
            skLineSegment(sketch, "E144", {"start": v(-3898.9, 254) * mm, "end": v(-3644.9, 254) * mm});
            skLineSegment(sketch, "E145", {"start": v(-3644.9, 254) * mm, "end": v(-3644.9, 0) * mm, "construction": true});
            skSolve(sketch);
        }
        {
            var Q0;
            Q0 = qSketchRegion(id + "F33", true);
            extrude(context, id + "F34", {"entities" : qUnion([Q0]), "operationType" : NewBodyOperationType.REMOVE, "oppositeDirection" : true, "depth" : 762 * mm});
        }
        {
            var Q0;
            Q0=makeQuery(id+"F26.boolean.opBoolean","MERGE",FACE,{"derivedFrom":[makeQuery(id+"F24.boolean.opBoolean","MERGE",FACE,{"derivedFrom":[makeQuery(id+"F1.opExtrude","CAP_FACE",FACE,{"disambiguationData":[OSD([sQuery(id+"F0.wireOp",EDGE,"E0.bottom"),sQuery(id+"F0.wireOp",EDGE,"E0.top"),sQuery(id+"F0.wireOp",EDGE,"E0.left"),sQuery(id+"F0.wireOp",EDGE,"E0.right")])],"isStart":true}),makeQuery(id+"F24.opExtrude","CAP_FACE",FACE,{"disambiguationData":[OSD([sQuery(id+"F23.wireOp",EDGE,"E119.0.0"),sQuery(id+"F23.wireOp",EDGE,"E119.0.1"),sQuery(id+"F23.wireOp",EDGE,"E119.0.2"),sQuery(id+"F23.wireOp",EDGE,"E119.0.3"),sQuery(id+"F23.wireOp",EDGE,"E120.0"),sQuery(id+"F23.wireOp",EDGE,"E120.1"),sQuery(id+"F23.wireOp",EDGE,"E120.2"),sQuery(id+"F23.wireOp",EDGE,"E120.3")])],"isStart":true})]}),makeQuery(id+"F26.opExtrude","SWEPT_FACE",FACE,{"disambiguationData":[OSD([sQuery(id+"F25.wireOp",EDGE,"E121.bottom")])]})]});
            var sketch = newSketch(context, id + "F35", { "sketchPlane" : qUnion([Q0])});
            skLineSegment(sketch, "E146.bottom", {"start": v(3822.7, 2146.3) * mm, "end": v(5041.9, 2146.3) * mm});
            skLineSegment(sketch, "E146.top", {"start": v(3822.7, 1384.3) * mm, "end": v(5041.9, 1384.3) * mm});
            skLineSegment(sketch, "E146.left", {"start": v(3822.7, 2146.3) * mm, "end": v(3822.7, 1384.3) * mm});
            skLineSegment(sketch, "E146.right", {"start": v(5041.9, 2146.3) * mm, "end": v(5041.9, 1384.3) * mm});
            skCircle(sketch, "E147", {"center": v(5041.9, 1765.3) * mm, "radius": 114.3 * mm});
            skLineSegment(sketch, "E148.bottom", {"start": v(5041.9, 1739.9) * mm, "end": v(5194.3, 1739.9) * mm, "construction": true});
            skLineSegment(sketch, "E148.top", {"start": v(5041.9, 1790.7) * mm, "end": v(5194.3, 1790.7) * mm, "construction": true});
            skLineSegment(sketch, "E148.left", {"start": v(5041.9, 1790.7) * mm, "end": v(5041.9, 1739.9) * mm, "construction": true});
            skLineSegment(sketch, "E148.right", {"start": v(5194.3, 1790.7) * mm, "end": v(5194.3, 1739.9) * mm, "construction": true});
            skLineSegment(sketch, "E149.bottom", {"start": v(5041.9, 1790.7) * mm, "end": v(4432.3, 1790.7) * mm, "construction": true});
            skLineSegment(sketch, "E149.top", {"start": v(5041.9, 1739.9) * mm, "end": v(4432.3, 1739.9) * mm, "construction": true});
            skLineSegment(sketch, "E149.right", {"start": v(4432.3, 1790.7) * mm, "end": v(4432.3, 1739.9) * mm, "construction": true});
            skCircle(sketch, "E150", {"center": v(4432.3, 1765.3) * mm, "radius": 114.3 * mm, "construction": true});
            skLineSegment(sketch, "E151.0", {"start": v(3644.9, 2247.9) * mm, "end": v(3644.9, 3009.9) * mm, "construction": true});
            skLineSegment(sketch, "E152.0", {"start": v(3644.9, 2247.9) * mm, "end": v(5295.9, 2247.9) * mm, "construction": true});
            skLineSegment(sketch, "E153.0", {"start": v(5295.9, 4406.9) * mm, "end": v(5295.9, 2247.9) * mm, "construction": true});
            skLineSegment(sketch, "E154.0", {"start": v(3644.9, 3009.9) * mm, "end": v(4533.9, 3009.9) * mm, "construction": true});
            skSolve(sketch);
        }
        {
            var Q0;
            Q0 = qSketchRegion(id + "F35", true);
            extrude(context, id + "F36", {"entities" : qUnion([Q0]), "operationType" : NewBodyOperationType.ADD, "depth" : 25.4 * mm});
        }
    });
